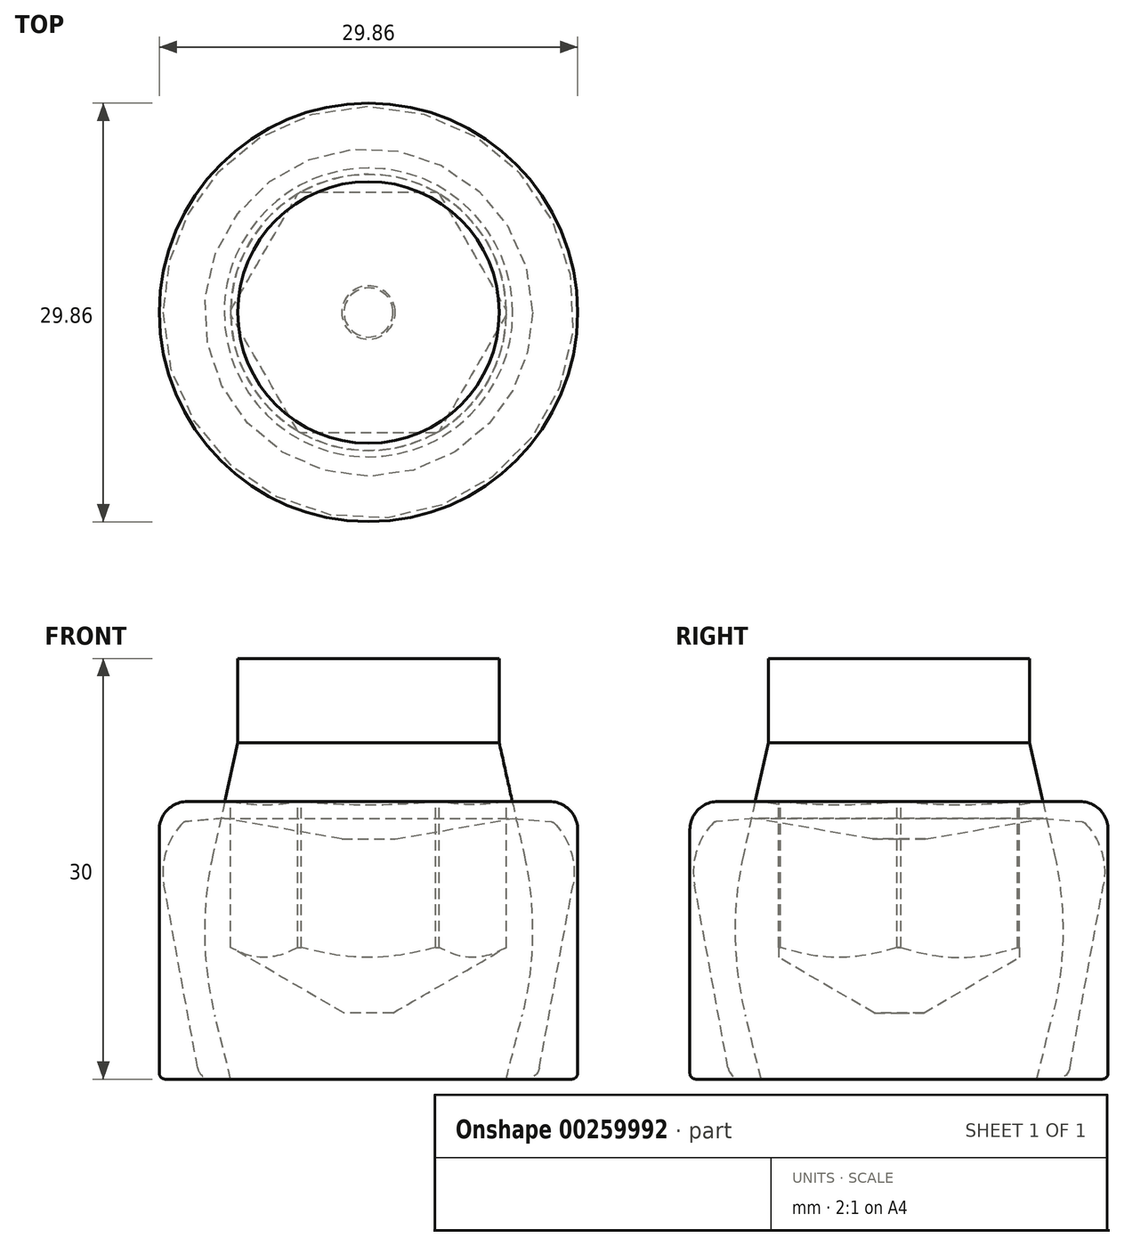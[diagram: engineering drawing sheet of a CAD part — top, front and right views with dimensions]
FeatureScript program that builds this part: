
annotation { "Feature Type Name" : "Feature", "Feature Type Description" : "" }
export const myFeature = defineFeature(function(context is Context, id is Id, definition is map)
    precondition{}
    {
        {
            var Q0;
            Q0=qCreatedBy(makeId("Front.planeOp"),FACE);
            var sketch = newSketch(context, id + "F0", { "sketchPlane" : qUnion([Q0])});
            skLineSegment(sketch, "E0", {"start": v(0, 0) * mm, "end": v(0, 4.72) * mm, "construction": true});
            skLineSegment(sketch, "E1", {"start": v(9.85, 19.8) * mm, "end": v(12.92, 19.8) * mm});
            skLineSegment(sketch, "E2", {"start": v(14.92, 17.8) * mm, "end": v(14.93, 0.43) * mm});
            skLineSegment(sketch, "E3", {"start": v(14.5, 0) * mm, "end": v(0, 0) * mm});
            skPoint(sketch, "E4.visualSharp", {"position": v(14.92, 19.8) * mm});
            skArc(sketch, "E4.filletArc", {"start": v(14.92, 17.8) * mm, "mid": v(14.34, 19.21) * mm, "end": v(12.92, 19.8) * mm});
            skPoint(sketch, "E5.visualSharp", {"position": v(14.93, 0) * mm});
            skArc(sketch, "E5.filletArc", {"start": v(14.5, 0) * mm, "mid": v(14.8, 0.12) * mm, "end": v(14.93, 0.43) * mm});
            skLineSegment(sketch, "E6", {"start": v(9.85, 19.8) * mm, "end": v(9.85, 9.4) * mm});
            skLineSegment(sketch, "E7", {"start": v(9.85, 9.4) * mm, "end": v(1.75, 4.72) * mm});
            skLineSegment(sketch, "E8", {"start": v(1.75, 4.72) * mm, "end": v(0, 4.72) * mm});
            skLineSegment(sketch, "E9", {"start": v(0, 4.72) * mm, "end": v(0, 0) * mm});
            skSolve(sketch);
        }
        {
            var Q0;
            Q0=qSketchRegion(id+"F0",true);
            var Q1;
            Q1=sQuery(id+"F0.wireOp",EDGE,"E9");
            revolve(context, id + "F1", {"surfaceOperationType" : NewSurfaceOperationType.NEW, "entities" : qUnion([Q0]), "axis" : qUnion([Q1]), "revolveType" : RevolveType.FULL});
        }
        {
            var Q0;
            Q0=makeQuery(id+"F1.opRevolve","SWEPT_FACE",FACE,{"disambiguationData":[OSD([sQuery(id+"F0.wireOp",EDGE,"E1")])]});
            var sketch = newSketch(context, id + "F2", { "sketchPlane" : qUnion([Q0])});
            skCircle(sketch, "E10", {"center": v(0, 0) * mm, "radius": 12.92 * mm});
            skCircle(sketch, "E11.cCircle", {"center": v(0, 0) * mm, "radius": 8.6 * mm, "construction": true});
            skLineSegment(sketch, "E11.0", {"start": v(-4.97, 8.6) * mm, "end": v(4.97, 8.6) * mm});
            skLineSegment(sketch, "E11.1", {"start": v(4.97, 8.6) * mm, "end": v(9.93, 0) * mm});
            skLineSegment(sketch, "E11.2", {"start": v(9.93, 0) * mm, "end": v(4.97, -8.6) * mm});
            skLineSegment(sketch, "E11.3", {"start": v(4.97, -8.6) * mm, "end": v(-4.97, -8.6) * mm});
            skLineSegment(sketch, "E11.4", {"start": v(-4.97, -8.6) * mm, "end": v(-9.93, 0) * mm});
            skLineSegment(sketch, "E11.5", {"start": v(-9.93, 0) * mm, "end": v(-4.97, 8.6) * mm});
            skPoint(sketch, "E11.0.midPoint", {"position": v(0, 8.6) * mm});
            skSolve(sketch);
        }
        {
            var Q0;
            Q0=qSketchRegion(id+"F2",true);
            var Q1;
            Q1=makeQuery(id+"F1.opRevolve","SWEPT_FACE",FACE,{"disambiguationData":[OSD([sQuery(id+"F0.wireOp",EDGE,"E7")])]});
            extrude(context, id + "F3", {"entities" : qUnion([Q0]), "operationType" : NewBodyOperationType.ADD, "endBound" : BoundingType.UP_TO_SURFACE, "oppositeDirection" : true, "endBoundEntityFace" : qUnion([Q1]), "depth" : 25 * mm});
        }
        {
            var Q0;
            Q0=makeQuery(id+"F3.boolean.opBoolean","MERGE",FACE,{"derivedFrom":[makeQuery(id+"F1.opRevolve","SWEPT_FACE",FACE,{"disambiguationData":[OSD([sQuery(id+"F0.wireOp",EDGE,"E1")])]}),makeQuery(id+"F3.opExtrude","CAP_FACE",FACE,{"disambiguationData":[OSD([sQuery(id+"F2.wireOp",EDGE,"axiUSiGf-8ymJ-Ezfh-tHsk-ULXXzRlxOoBz"),sQuery(id+"F2.wireOp",EDGE,"WrdyBTnM-XU54-uk96-2Sjo-h1HHDxb1zyqn"),sQuery(id+"F2.wireOp",EDGE,"7iNK7enz-fUzD-7EQp-KRCh-aPKnPlRcPdaK"),sQuery(id+"F2.wireOp",EDGE,"e7c95674-c634-4135-8625-61586754ee6a.1.0"),sQuery(id+"F2.wireOp",EDGE,"e7c95674-c634-4135-8625-61586754ee6a.1.1"),sQuery(id+"F2.wireOp",EDGE,"e7c95674-c634-4135-8625-61586754ee6a.1.2"),sQuery(id+"F2.wireOp",EDGE,"e7c95674-c634-4135-8625-61586754ee6a.2.0"),sQuery(id+"F2.wireOp",EDGE,"e7c95674-c634-4135-8625-61586754ee6a.2.1"),sQuery(id+"F2.wireOp",EDGE,"e7c95674-c634-4135-8625-61586754ee6a.2.2"),sQuery(id+"F2.wireOp",EDGE,"e7c95674-c634-4135-8625-61586754ee6a.3.0"),sQuery(id+"F2.wireOp",EDGE,"e7c95674-c634-4135-8625-61586754ee6a.3.1"),sQuery(id+"F2.wireOp",EDGE,"e7c95674-c634-4135-8625-61586754ee6a.3.2"),sQuery(id+"F2.wireOp",EDGE,"e7c95674-c634-4135-8625-61586754ee6a.4.0"),sQuery(id+"F2.wireOp",EDGE,"e7c95674-c634-4135-8625-61586754ee6a.4.1"),sQuery(id+"F2.wireOp",EDGE,"e7c95674-c634-4135-8625-61586754ee6a.4.2"),sQuery(id+"F2.wireOp",EDGE,"e7c95674-c634-4135-8625-61586754ee6a.5.0"),sQuery(id+"F2.wireOp",EDGE,"e7c95674-c634-4135-8625-61586754ee6a.5.1"),sQuery(id+"F2.wireOp",EDGE,"e7c95674-c634-4135-8625-61586754ee6a.5.2"),sQuery(id+"F2.wireOp",EDGE,"c34f7dbc-1fd9-48ae-9599-0fb72b0d65de.filletArc"),sQuery(id+"F2.wireOp",EDGE,"5fecc0f4-c57f-42b8-a97f-f8fbf54cf4db.filletArc"),sQuery(id+"F2.wireOp",EDGE,"b077568f-b672-48a6-a184-fa18c1575088.filletArc"),sQuery(id+"F2.wireOp",EDGE,"4c4ba650-eb3b-40a6-a5b6-7d0bcd232093.filletArc"),sQuery(id+"F2.wireOp",EDGE,"b016cc09-0b8d-437b-9508-1d7630c9d4ff.filletArc"),sQuery(id+"F2.wireOp",EDGE,"d5479cb3-145b-41e2-b586-5ab3f6452500.filletArc"),sQuery(id+"F2.wireOp",EDGE,"E10")])],"isStart":true})]});
            var sketch = newSketch(context, id + "F4", { "sketchPlane" : qUnion([Q0])});
            skCircle(sketch, "E12", {"center": v(0, 0) * mm, "radius": 9.85 * mm});
            skSolve(sketch);
        }
        {
            var Q0;
            Q0=qSketchRegion(id+"F4",true);
            extrude(context, id + "F5", {"entities" : qUnion([Q0]), "operationType" : NewBodyOperationType.REMOVE, "oppositeDirection" : true, "depth" : 1 * mm, "hasDraft" : true, "draftAngle" : 80 * degree, "draftPullDirection" : true});
        }
        {
            var Q0;
            Q0=qCreatedBy(makeId("Front.planeOp"),FACE);
            var sketch = newSketch(context, id + "F6", { "sketchPlane" : qUnion([Q0])});
            skLineSegment(sketch, "E13", {"start": v(0, 0) * mm, "end": v(0, 30) * mm, "construction": true});
            skLineSegment(sketch, "E14", {"start": v(0, 30) * mm, "end": v(9.33, 30) * mm});
            skLineSegment(sketch, "E15", {"start": v(9.33, 30) * mm, "end": v(9.33, 24) * mm});
            skLineSegment(sketch, "E16", {"start": v(9.33, 24) * mm, "end": v(11.1, 15.98) * mm});
            skLineSegment(sketch, "E17", {"start": v(9.83, 0) * mm, "end": v(0, 0) * mm});
            skLineSegment(sketch, "E18", {"start": v(0, 30) * mm, "end": v(0, 0) * mm});
            skLineSegment(sketch, "E19", {"start": v(9.83, 0) * mm, "end": v(10.96, 4.52) * mm});
            skArc(sketch, "E20.filletArc", {"start": v(10.96, 4.52) * mm, "mid": v(11.7, 10.24) * mm, "end": v(11.1, 15.98) * mm});
            skLineSegment(sketch, "E21", {"start": v(9.33, 24) * mm, "end": v(11.55, 14) * mm, "construction": true});
            skLineSegment(sketch, "E22", {"start": v(9.83, 0) * mm, "end": v(12.07, 9) * mm, "construction": true});
            skSolve(sketch);
        }
        {
            var Q0;
            Q0=qSketchRegion(id+"F6",true);
            var Q1;
            Q1=sQuery(id+"F6.wireOp",EDGE,"E18");
            revolve(context, id + "F7", {"entities" : qUnion([Q0]), "axis" : qUnion([Q1]), "revolveType" : RevolveType.FULL});
        }
        {
            var Q0;
            Q0=qCreatedBy(makeId("Front.planeOp"),FACE);
            var sketch = newSketch(context, id + "F8", { "sketchPlane" : qUnion([Q0])});
            skLineSegment(sketch, "E23", {"start": v(0, 0) * mm, "end": v(0, 17.12) * mm});
            skLineSegment(sketch, "E24", {"start": v(14.6, 13.87) * mm, "end": v(12.2, 0.82) * mm});
            skLineSegment(sketch, "E25", {"start": v(11.21, 0) * mm, "end": v(0, 0) * mm});
            skPoint(sketch, "E26.visualSharp", {"position": v(12.05, 0) * mm});
            skArc(sketch, "E26.filletArc", {"start": v(11.21, 0) * mm, "mid": v(11.85, 0.23) * mm, "end": v(12.2, 0.82) * mm});
            skLineSegment(sketch, "E27", {"start": v(0, 17.12) * mm, "end": v(0, 0) * mm, "construction": true});
            skLineSegment(sketch, "E28", {"start": v(0, 17.12) * mm, "end": v(1.9, 17.12) * mm});
            skLineSegment(sketch, "E29", {"start": v(1.9, 17.12) * mm, "end": v(10.3, 18.6) * mm});
            skLineSegment(sketch, "E30", {"start": v(10.3, 18.6) * mm, "end": v(13.06, 18.36) * mm});
            skArc(sketch, "E31.filletArc", {"start": v(14.6, 13.87) * mm, "mid": v(14.46, 16.23) * mm, "end": v(13.25, 18.27) * mm});
            skPoint(sketch, "E32.visualSharp", {"position": v(13.17, 18.35) * mm});
            skArc(sketch, "E32.filletArc", {"start": v(13.25, 18.27) * mm, "mid": v(13.16, 18.33) * mm, "end": v(13.06, 18.36) * mm});
            skLineSegment(sketch, "E33", {"start": v(14.6, 13.87) * mm, "end": v(14.8, 15) * mm, "construction": true});
            skSolve(sketch);
        }
        {
            var Q0;
            Q0=qSketchRegion(id+"F8",true);
            var Q1;
            Q1=sQuery(id+"F8.wireOp",EDGE,"E23");
            revolve(context, id + "F9", {"entities" : qUnion([Q0]), "axis" : qUnion([Q1]), "revolveType" : RevolveType.FULL});
        }
    });
